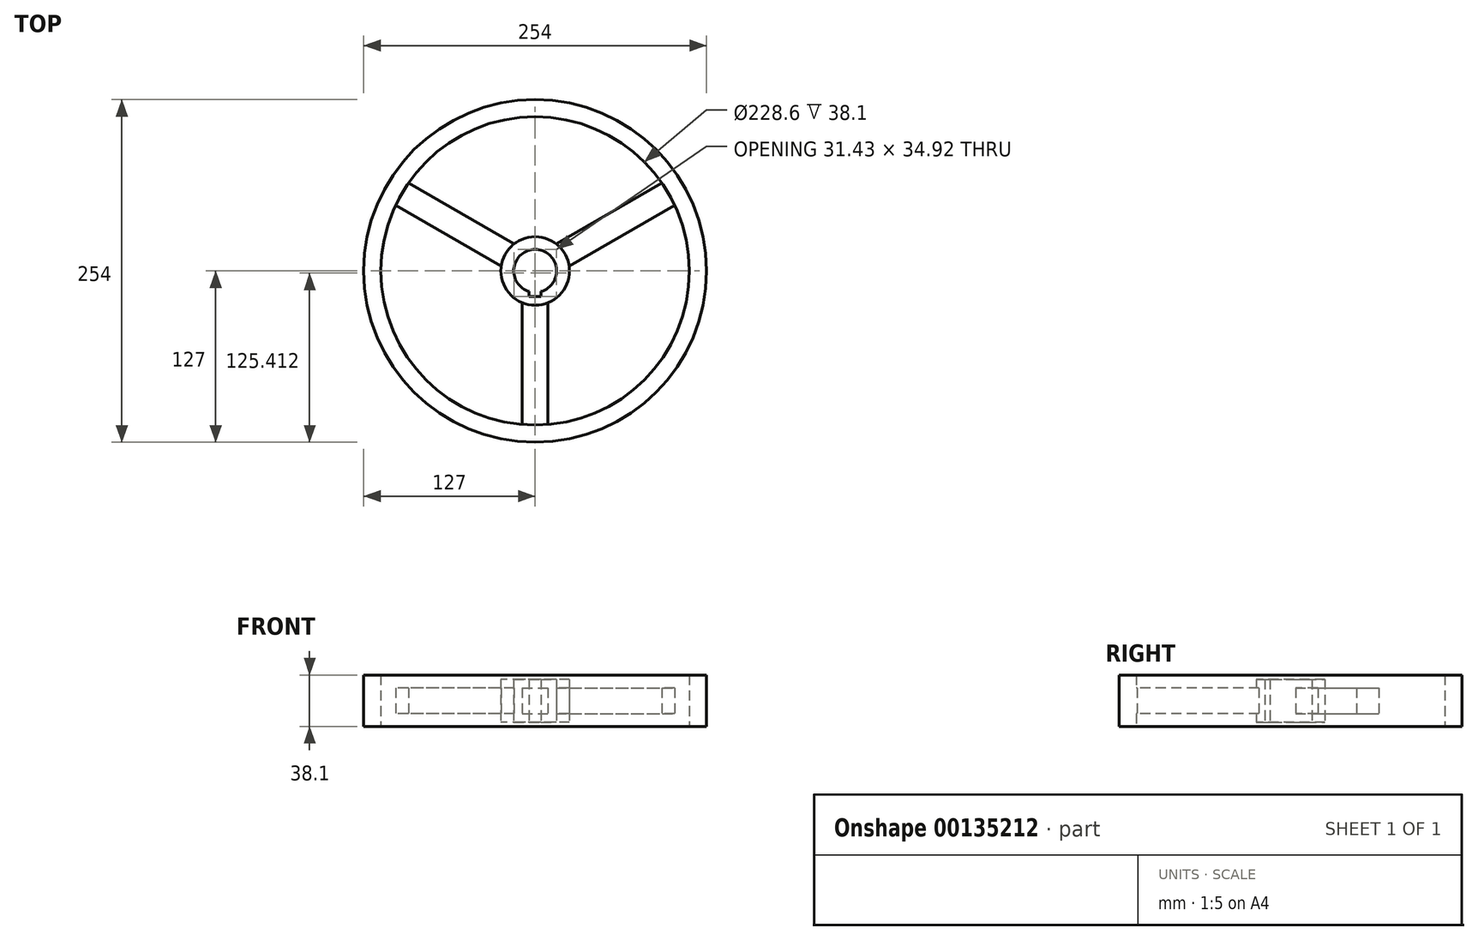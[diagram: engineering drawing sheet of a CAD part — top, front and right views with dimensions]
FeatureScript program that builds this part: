
annotation { "Feature Type Name" : "Feature", "Feature Type Description" : "" }
export const myFeature = defineFeature(function(context is Context, id is Id, definition is map)
    precondition{}
    {
        {
            var Q0;
            Q0=qCreatedBy(makeId("Top.planeOp"),FACE);
            var sketch = newSketch(context, id + "F0", { "sketchPlane" : qUnion([Q0])});
            skCircle(sketch, "E0", {"center": v(0, 0) * mm, "radius": 127 * mm});
            skCircle(sketch, "E1", {"center": v(0, 0) * mm, "radius": 114.3 * mm});
            skCircle(sketch, "E2", {"center": v(0, 0) * mm, "radius": 25.4 * mm});
            skArc(sketch, "E3", {"start": v(4.45, -15.24) * mm, "mid": v(0, 15.88) * mm, "end": v(-4.45, -15.24) * mm});
            skLineSegment(sketch, "E4", {"start": v(-4.45, -15.24) * mm, "end": v(-4.45, -19.05) * mm});
            skLineSegment(sketch, "E5", {"start": v(-4.45, -19.05) * mm, "end": v(4.45, -19.05) * mm});
            skLineSegment(sketch, "E6", {"start": v(4.45, -19.05) * mm, "end": v(4.45, -15.24) * mm});
            skLineSegment(sketch, "E7", {"start": v(-9.53, -23.55) * mm, "end": v(-9.53, -113.9) * mm});
            skLineSegment(sketch, "E8.MirrorCS", {"start": v(9.53, -23.55) * mm, "end": v(9.53, -113.9) * mm});
            skLineSegment(sketch, "E9.1.0", {"start": v(-15.63, 20.02) * mm, "end": v(-93.88, 65.2) * mm});
            skLineSegment(sketch, "E9.1.1", {"start": v(-25.15, 3.52) * mm, "end": v(-103.4, 48.7) * mm});
            skLineSegment(sketch, "E9.2.0", {"start": v(25.15, 3.52) * mm, "end": v(103.4, 48.7) * mm});
            skLineSegment(sketch, "E9.2.1", {"start": v(15.63, 20.02) * mm, "end": v(93.88, 65.2) * mm});
            skLineSegment(sketch, "E9.anchor1", {"start": v(0, 0) * mm, "end": v(-9.53, -113.9) * mm, "construction": true});
            skLineSegment(sketch, "E9.anchor2", {"start": v(0, 0) * mm, "end": v(103.4, 48.7) * mm, "construction": true});
            skSolve(sketch);
        }
        {
            var Q0;
            Q0=makeQuery(id+"F0.imprint","IMPRINT",FACE,{"disambiguationData":[TD([[makeQuery(id+"F0.imprint","IMPRINT",EDGE,{"derivedFrom":sQuery(id+"F0.wireOp",EDGE,"E3")}),-1.0]])]});
            extrude(context, id + "F1", {"entities" : qUnion([Q0]), "endBound" : BoundingType.SYMMETRIC, "depth" : 31.75 * mm});
        }
        {
            var Q0;
            {var subQ0=sQuery(id+"F0.wireOp",EDGE,"E9.1.0");Q0=makeQuery(id+"F0.imprint","IMPRINT",FACE,{"disambiguationData":[TD([[makeQuery(id+"F0.imprint","IMPRINT",EDGE,{"derivedFrom":subQ0}),1.0]])]});}
            var Q1;
            {var subQ0=sQuery(id+"F0.wireOp",EDGE,"E9.2.0");Q1=makeQuery(id+"F0.imprint","IMPRINT",FACE,{"disambiguationData":[TD([[makeQuery(id+"F0.imprint","IMPRINT",EDGE,{"derivedFrom":subQ0}),1.0]])]});}
            var Q2;
            {var subQ0=sQuery(id+"F0.wireOp",EDGE,"E7");Q2=makeQuery(id+"F0.imprint","IMPRINT",FACE,{"disambiguationData":[TD([[makeQuery(id+"F0.imprint","IMPRINT",EDGE,{"derivedFrom":subQ0}),1.0]])]});}
            extrude(context, id + "F2", {"entities" : qUnion([Q0, Q1, Q2]), "operationType" : NewBodyOperationType.ADD, "endBound" : BoundingType.SYMMETRIC, "depth" : 19.05 * mm});
        }
        {
            var Q0;
            Q0=makeQuery(id+"F0.imprint","IMPRINT",FACE,{"disambiguationData":[TD([[makeQuery(id+"F0.imprint","IMPRINT",EDGE,{"derivedFrom":sQuery(id+"F0.wireOp",EDGE,"E0")}),1.0]])]});
            extrude(context, id + "F3", {"entities" : qUnion([Q0]), "operationType" : NewBodyOperationType.ADD, "endBound" : BoundingType.SYMMETRIC, "depth" : 38.1 * mm});
        }
    });
